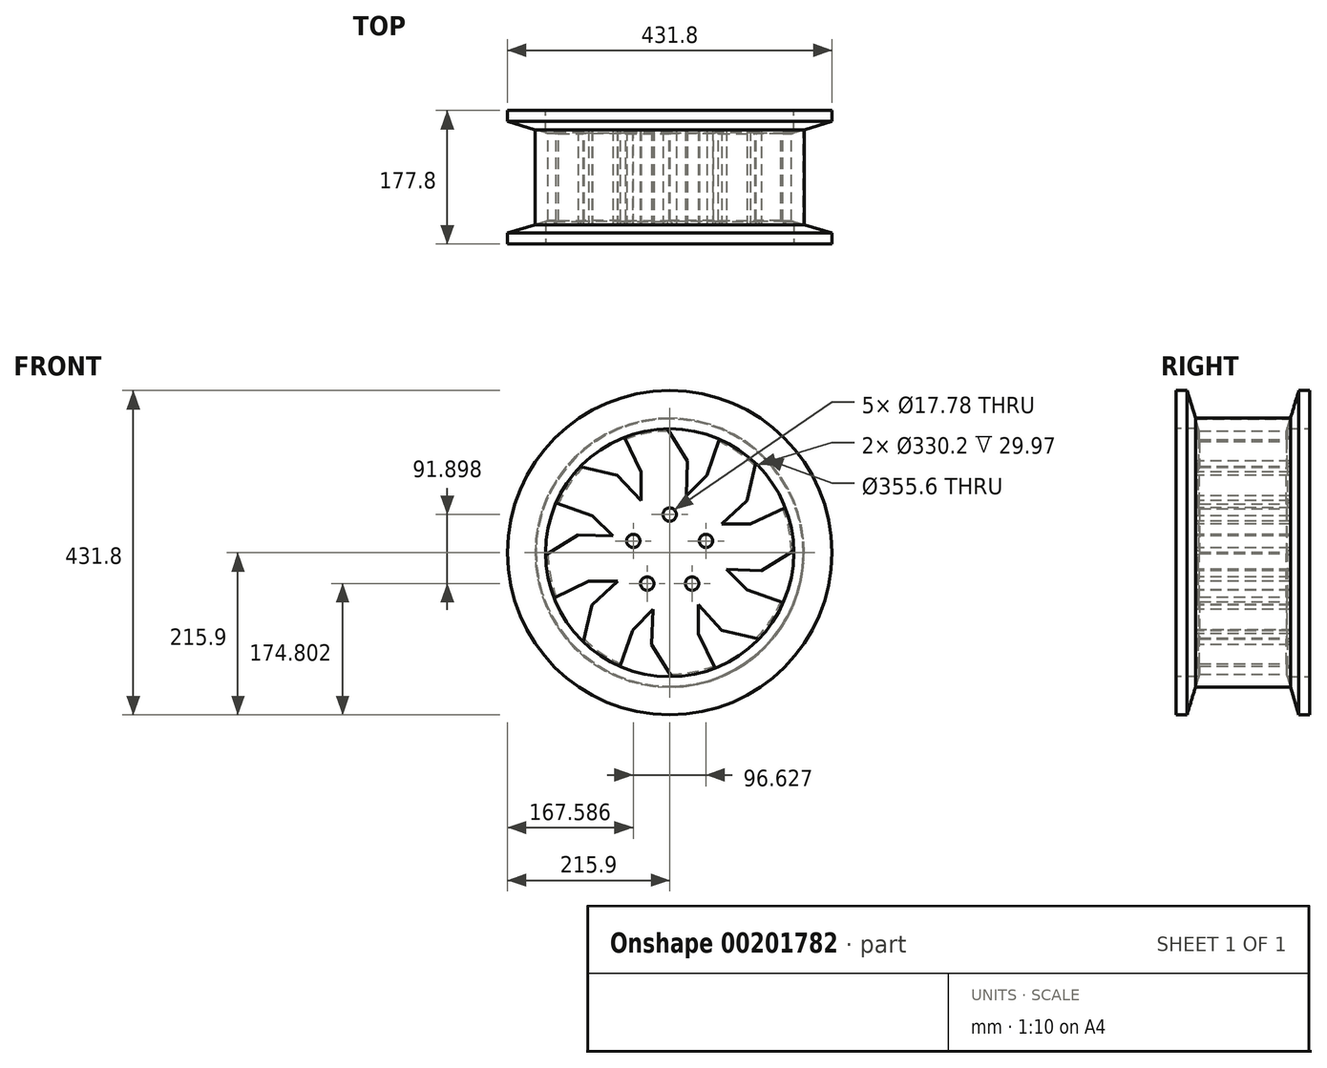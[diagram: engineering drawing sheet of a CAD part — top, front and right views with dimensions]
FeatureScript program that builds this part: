
annotation { "Feature Type Name" : "Feature", "Feature Type Description" : "" }
export const myFeature = defineFeature(function(context is Context, id is Id, definition is map)
    precondition{}
    {
        {
            var Q0;
            Q0=qCreatedBy(makeId("Front.planeOp"),FACE);
            var sketch = newSketch(context, id + "F0", { "sketchPlane" : qUnion([Q0])});
            skCircle(sketch, "E0", {"center": v(0, 0) * mm, "radius": 215.9 * mm});
            skSolve(sketch);
        }
        {
            var Q0;
            Q0 = qSketchRegion(id + "F0", true);
            extrude(context, id + "F1", {"entities" : qUnion([Q0]), "oppositeDirection" : true, "depth" : 177.8 * mm});
        }
        {
            var Q0;
            Q0=qCreatedBy(makeId("Right.planeOp"),FACE);
            var sketch = newSketch(context, id + "F2", { "sketchPlane" : qUnion([Q0])});
            skLineSegment(sketch, "E1", {"start": v(12.27, 222.89) * mm, "end": v(30.99, 161.77) * mm});
            skLineSegment(sketch, "E2", {"start": v(30.99, 161.77) * mm, "end": v(85.04, 161.77) * mm});
            skLineSegment(sketch, "E3", {"start": v(88.9, 247.97) * mm, "end": v(88.9, 109.84) * mm});
            skLineSegment(sketch, "E4", {"start": v(85.04, 161.77) * mm, "end": v(88.9, 161.77) * mm});
            skLineSegment(sketch, "E5", {"start": v(12.27, 222.89) * mm, "end": v(88.9, 222.89) * mm});
            skLineSegment(sketch, "E6.MirrorCS", {"start": v(165.53, 222.89) * mm, "end": v(88.9, 222.89) * mm});
            skLineSegment(sketch, "E7.MirrorCS", {"start": v(165.53, 222.89) * mm, "end": v(146.81, 161.77) * mm});
            skLineSegment(sketch, "E8.MirrorCS", {"start": v(146.81, 161.77) * mm, "end": v(92.76, 161.77) * mm});
            skLineSegment(sketch, "E9.MirrorCS", {"start": v(92.76, 161.77) * mm, "end": v(88.9, 161.77) * mm});
            skSolve(sketch);
        }
        {
            var Q0;
            Q0=qCreatedBy(makeId("Right.planeOp"),FACE);
            var sketch = newSketch(context, id + "F3", { "sketchPlane" : qUnion([Q0])});
            skLineSegment(sketch, "E10", {"start": v(0, 0) * mm, "end": v(269.37, 0) * mm});
            skSolve(sketch);
        }
        {
            var Q0;
            {var subQ0=sQuery(id+"F2.wireOp",EDGE,"E6.MirrorCS");Q0=makeQuery(id+"F2.imprint","IMPRINT",FACE,{"disambiguationData":[TD([[makeQuery(id+"F2.imprint","IMPRINT",EDGE,{"derivedFrom":subQ0}),1.0]])]});}
            var Q1;
            Q1=makeQuery(id+"F2.imprint","IMPRINT",FACE,{"disambiguationData":[TD([[makeQuery(id+"F2.imprint","IMPRINT",EDGE,{"derivedFrom":sQuery(id+"F2.wireOp",EDGE,"E1")}),1.0]])]});
            var Q2;
            Q2=sQuery(id+"F3.wireOp",EDGE,"E10");
            revolve(context, id + "F4", {"operationType" : NewBodyOperationType.REMOVE, "entities" : qUnion([Q0, Q1]), "axis" : qUnion([Q2]), "revolveType" : RevolveType.FULL, "oppositeDirection" : true});
        }
        {
            var Q0;
            Q0=makeQuery(id+"F1.opExtrude","CAP_FACE",FACE,{"disambiguationData":[OSD([sQuery(id+"F0.wireOp",EDGE,"E0")])],"isStart":true});
            var sketch = newSketch(context, id + "F5", { "sketchPlane" : qUnion([Q0])});
            skCircle(sketch, "E11", {"center": v(0, 0) * mm, "radius": 165.1 * mm});
            skSolve(sketch);
        }
        {
            var Q0;
            Q0 = qSketchRegion(id + "F5", true);
            extrude(context, id + "F6", {"entities" : qUnion([Q0]), "operationType" : NewBodyOperationType.REMOVE, "oppositeDirection" : true, "depth" : 25.4 * mm});
        }
        {
            var Q0;
            Q0=makeQuery(id+"F1.opExtrude","CAP_FACE",FACE,{"disambiguationData":[OSD([sQuery(id+"F0.wireOp",EDGE,"E0")])],"isStart":false});
            var sketch = newSketch(context, id + "F7", { "sketchPlane" : qUnion([Q0])});
            skCircle(sketch, "E12", {"center": v(0, 0) * mm, "radius": 165.1 * mm});
            skSolve(sketch);
        }
        {
            var Q0;
            Q0 = qSketchRegion(id + "F7", true);
            extrude(context, id + "F8", {"entities" : qUnion([Q0]), "operationType" : NewBodyOperationType.REMOVE, "oppositeDirection" : true, "depth" : 25.4 * mm});
        }
        {
            var Q0;
            Q0=makeQuery(id+"F6.boolean.opBoolean","COPY",FACE,{"derivedFrom":makeQuery(id+"F6.opExtrude","CAP_FACE",FACE,{"disambiguationData":[OSD([sQuery(id+"F5.wireOp",EDGE,"E11")])],"isStart":false})});
            var sketch = newSketch(context, id + "F9", { "sketchPlane" : qUnion([Q0])});
            skCircle(sketch, "E13", {"center": v(0, 50.8) * mm, "radius": 8.9 * mm});
            skCircle(sketch, "E14.1.0", {"center": v(-48.31, 15.7) * mm, "radius": 8.9 * mm});
            skCircle(sketch, "E14.2.0", {"center": v(-29.86, -41.1) * mm, "radius": 8.9 * mm});
            skCircle(sketch, "E14.3.0", {"center": v(29.86, -41.1) * mm, "radius": 8.9 * mm});
            skCircle(sketch, "E14.4.0", {"center": v(48.31, 15.7) * mm, "radius": 8.9 * mm});
            skPoint(sketch, "E14.center", {"position": v(0, 0) * mm});
            skSolve(sketch);
        }
        {
            var Q0;
            Q0 = qSketchRegion(id + "F9", true);
            extrude(context, id + "F10", {"entities" : qUnion([Q0]), "operationType" : NewBodyOperationType.REMOVE, "endBound" : BoundingType.THROUGH_ALL, "oppositeDirection" : true, "depth" : 25.4 * mm});
        }
        {
            var Q0;
            Q0=makeQuery(id+"F1.opExtrude","CAP_FACE",FACE,{"disambiguationData":[OSD([sQuery(id+"F0.wireOp",EDGE,"E0")])],"isStart":false});
            var sketch = newSketch(context, id + "F11", { "sketchPlane" : qUnion([Q0])});
            skCircle(sketch, "E15", {"center": v(0, 0) * mm, "radius": 177.8 * mm});
            skCircle(sketch, "E16", {"center": v(0, 0) * mm, "radius": 179.07 * mm});
            skSolve(sketch);
        }
        {
            var Q0;
            Q0 = qSketchRegion(id + "F11", true);
            extrude(context, id + "F12", {"entities" : qUnion([Q0]), "operationType" : NewBodyOperationType.ADD, "oppositeDirection" : true, "depth" : 158.75 * mm});
        }
        {
            var Q0;
            Q0=makeQuery(id+"F6.boolean.opBoolean","COPY",FACE,{"derivedFrom":makeQuery(id+"F6.opExtrude","CAP_FACE",FACE,{"disambiguationData":[OSD([sQuery(id+"F5.wireOp",EDGE,"E11")])],"isStart":false})});
            var sketch = newSketch(context, id + "F13", { "sketchPlane" : qUnion([Q0])});
            skLineSegment(sketch, "E17", {"start": v(-60.1, 153.77) * mm, "end": v(-37.94, 107.65) * mm});
            skLineSegment(sketch, "E18", {"start": v(-37.94, 69.14) * mm, "end": v(-69.59, 103.17) * mm});
            skLineSegment(sketch, "E19", {"start": v(-37.94, 107.65) * mm, "end": v(-37.94, 69.14) * mm});
            skLineSegment(sketch, "E20", {"start": v(-69.59, 103.17) * mm, "end": v(-118.77, 114.68) * mm});
            skArc(sketch, "E21", {"start": v(-118.77, 114.68) * mm, "mid": v(-91.55, 137.4) * mm, "end": v(-60.1, 153.77) * mm});
            skLineSegment(sketch, "E22.1.0", {"start": v(-122.16, 23.75) * mm, "end": v(-165.07, -2.9) * mm});
            skLineSegment(sketch, "E22.1.1", {"start": v(-102.95, 49.29) * mm, "end": v(-75.72, 22.06) * mm});
            skArc(sketch, "E22.1.2", {"start": v(-165.07, -2.9) * mm, "mid": v(-161.89, 32.42) * mm, "end": v(-151.23, 66.24) * mm});
            skLineSegment(sketch, "E22.1.3", {"start": v(-151.23, 66.24) * mm, "end": v(-102.95, 49.29) * mm});
            skLineSegment(sketch, "E22.1.4", {"start": v(-75.72, 22.06) * mm, "end": v(-122.16, 23.75) * mm});
            skLineSegment(sketch, "E22.2.0", {"start": v(-103.17, -69.59) * mm, "end": v(-114.68, -118.77) * mm});
            skLineSegment(sketch, "E22.2.1", {"start": v(-107.65, -37.94) * mm, "end": v(-69.14, -37.94) * mm});
            skArc(sketch, "E22.2.2", {"start": v(-114.68, -118.77) * mm, "mid": v(-137.4, -91.55) * mm, "end": v(-153.77, -60.1) * mm});
            skLineSegment(sketch, "E22.2.3", {"start": v(-153.77, -60.1) * mm, "end": v(-107.65, -37.94) * mm});
            skLineSegment(sketch, "E22.2.4", {"start": v(-69.14, -37.94) * mm, "end": v(-103.17, -69.59) * mm});
            skLineSegment(sketch, "E22.3.0", {"start": v(-23.75, -122.16) * mm, "end": v(2.9, -165.07) * mm});
            skLineSegment(sketch, "E22.3.1", {"start": v(-49.29, -102.95) * mm, "end": v(-22.06, -75.72) * mm});
            skArc(sketch, "E22.3.2", {"start": v(2.9, -165.07) * mm, "mid": v(-32.42, -161.89) * mm, "end": v(-66.24, -151.23) * mm});
            skLineSegment(sketch, "E22.3.3", {"start": v(-66.24, -151.23) * mm, "end": v(-49.29, -102.95) * mm});
            skLineSegment(sketch, "E22.3.4", {"start": v(-22.06, -75.72) * mm, "end": v(-23.75, -122.16) * mm});
            skLineSegment(sketch, "E22.4.0", {"start": v(69.59, -103.17) * mm, "end": v(118.77, -114.68) * mm});
            skLineSegment(sketch, "E22.4.1", {"start": v(37.94, -107.65) * mm, "end": v(37.94, -69.14) * mm});
            skArc(sketch, "E22.4.2", {"start": v(118.77, -114.68) * mm, "mid": v(91.55, -137.4) * mm, "end": v(60.1, -153.77) * mm});
            skLineSegment(sketch, "E22.4.3", {"start": v(60.1, -153.77) * mm, "end": v(37.94, -107.65) * mm});
            skLineSegment(sketch, "E22.4.4", {"start": v(37.94, -69.14) * mm, "end": v(69.59, -103.17) * mm});
            skLineSegment(sketch, "E22.5.0", {"start": v(122.16, -23.75) * mm, "end": v(165.07, 2.9) * mm});
            skLineSegment(sketch, "E22.5.1", {"start": v(102.95, -49.29) * mm, "end": v(75.72, -22.06) * mm});
            skArc(sketch, "E22.5.2", {"start": v(165.07, 2.9) * mm, "mid": v(161.89, -32.42) * mm, "end": v(151.23, -66.24) * mm});
            skLineSegment(sketch, "E22.5.3", {"start": v(151.23, -66.24) * mm, "end": v(102.95, -49.29) * mm});
            skLineSegment(sketch, "E22.5.4", {"start": v(75.72, -22.06) * mm, "end": v(122.16, -23.75) * mm});
            skLineSegment(sketch, "E22.6.0", {"start": v(103.17, 69.59) * mm, "end": v(114.68, 118.77) * mm});
            skLineSegment(sketch, "E22.6.1", {"start": v(107.65, 37.94) * mm, "end": v(69.14, 37.94) * mm});
            skArc(sketch, "E22.6.2", {"start": v(114.68, 118.77) * mm, "mid": v(137.4, 91.55) * mm, "end": v(153.77, 60.1) * mm});
            skLineSegment(sketch, "E22.6.3", {"start": v(153.77, 60.1) * mm, "end": v(107.65, 37.94) * mm});
            skLineSegment(sketch, "E22.6.4", {"start": v(69.14, 37.94) * mm, "end": v(103.17, 69.59) * mm});
            skLineSegment(sketch, "E22.7.0", {"start": v(23.75, 122.16) * mm, "end": v(-2.9, 165.07) * mm});
            skLineSegment(sketch, "E22.7.1", {"start": v(49.29, 102.95) * mm, "end": v(22.06, 75.72) * mm});
            skArc(sketch, "E22.7.2", {"start": v(-2.9, 165.07) * mm, "mid": v(32.42, 161.89) * mm, "end": v(66.24, 151.23) * mm});
            skLineSegment(sketch, "E22.7.3", {"start": v(66.24, 151.23) * mm, "end": v(49.29, 102.95) * mm});
            skLineSegment(sketch, "E22.7.4", {"start": v(22.06, 75.72) * mm, "end": v(23.75, 122.16) * mm});
            skSolve(sketch);
        }
        {
            var Q0;
            Q0 = qSketchRegion(id + "F13", true);
            extrude(context, id + "F14", {"entities" : qUnion([Q0]), "operationType" : NewBodyOperationType.REMOVE, "endBound" : BoundingType.THROUGH_ALL, "oppositeDirection" : true, "depth" : 25.4 * mm});
        }
        {
            var Q0;
            Q0=makeQuery(id+"F14.boolean.opBoolean","COPY",EDGE,{"derivedFrom":makeQuery(id+"F14.opExtrude","CAP_EDGE",EDGE,{"disambiguationData":[OSD([sQuery(id+"F13.wireOp",EDGE,"E20")])],"isStart":true})});
            var Q1;
            Q1=makeQuery(id+"F14.boolean.opBoolean","COPY",EDGE,{"derivedFrom":makeQuery(id+"F14.opExtrude","CAP_EDGE",EDGE,{"disambiguationData":[OSD([sQuery(id+"F13.wireOp",EDGE,"E18")])],"isStart":true})});
            var Q2;
            Q2=makeQuery(id+"F14.boolean.opBoolean","COPY",EDGE,{"derivedFrom":makeQuery(id+"F14.opExtrude","CAP_EDGE",EDGE,{"disambiguationData":[OSD([sQuery(id+"F13.wireOp",EDGE,"E19")])],"isStart":true})});
            var Q3;
            Q3=makeQuery(id+"F14.boolean.opBoolean","COPY",EDGE,{"derivedFrom":makeQuery(id+"F14.opExtrude","CAP_EDGE",EDGE,{"disambiguationData":[OSD([sQuery(id+"F13.wireOp",EDGE,"E17")])],"isStart":true})});
            var Q4;
            Q4=makeQuery(id+"F14.boolean.opBoolean","COPY",EDGE,{"derivedFrom":makeQuery(id+"F14.opExtrude","CAP_EDGE",EDGE,{"disambiguationData":[OSD([sQuery(id+"F13.wireOp",EDGE,"E22.7.0")])],"isStart":true})});
            var Q5;
            Q5=makeQuery(id+"F14.boolean.opBoolean","COPY",EDGE,{"derivedFrom":makeQuery(id+"F14.opExtrude","CAP_EDGE",EDGE,{"disambiguationData":[OSD([sQuery(id+"F13.wireOp",EDGE,"E22.7.4")])],"isStart":true})});
            var Q6;
            Q6=makeQuery(id+"F14.boolean.opBoolean","COPY",EDGE,{"derivedFrom":makeQuery(id+"F14.opExtrude","CAP_EDGE",EDGE,{"disambiguationData":[OSD([sQuery(id+"F13.wireOp",EDGE,"E22.7.1")])],"isStart":true})});
            var Q7;
            Q7=makeQuery(id+"F14.boolean.opBoolean","COPY",EDGE,{"derivedFrom":makeQuery(id+"F14.opExtrude","CAP_EDGE",EDGE,{"disambiguationData":[OSD([sQuery(id+"F13.wireOp",EDGE,"E22.7.3")])],"isStart":true})});
            var Q8;
            Q8=makeQuery(id+"F14.boolean.opBoolean","COPY",EDGE,{"derivedFrom":makeQuery(id+"F14.opExtrude","CAP_EDGE",EDGE,{"disambiguationData":[OSD([sQuery(id+"F13.wireOp",EDGE,"E22.6.4")])],"isStart":true})});
            var Q9;
            Q9=makeQuery(id+"F14.boolean.opBoolean","COPY",EDGE,{"derivedFrom":makeQuery(id+"F14.opExtrude","CAP_EDGE",EDGE,{"disambiguationData":[OSD([sQuery(id+"F13.wireOp",EDGE,"E22.6.1")])],"isStart":true})});
            var Q10;
            Q10=makeQuery(id+"F14.boolean.opBoolean","COPY",EDGE,{"derivedFrom":makeQuery(id+"F14.opExtrude","CAP_EDGE",EDGE,{"disambiguationData":[OSD([sQuery(id+"F13.wireOp",EDGE,"E22.6.3")])],"isStart":true})});
            var Q11;
            Q11=makeQuery(id+"F14.boolean.opBoolean","COPY",EDGE,{"derivedFrom":makeQuery(id+"F14.opExtrude","CAP_EDGE",EDGE,{"disambiguationData":[OSD([sQuery(id+"F13.wireOp",EDGE,"E22.6.0")])],"isStart":true})});
            var Q12;
            Q12=makeQuery(id+"F14.boolean.opBoolean","COPY",EDGE,{"derivedFrom":makeQuery(id+"F14.opExtrude","CAP_EDGE",EDGE,{"disambiguationData":[OSD([sQuery(id+"F13.wireOp",EDGE,"E22.5.0")])],"isStart":true})});
            var Q13;
            Q13=makeQuery(id+"F14.boolean.opBoolean","COPY",EDGE,{"derivedFrom":makeQuery(id+"F14.opExtrude","CAP_EDGE",EDGE,{"disambiguationData":[OSD([sQuery(id+"F13.wireOp",EDGE,"E22.5.4")])],"isStart":true})});
            var Q14;
            Q14=makeQuery(id+"F14.boolean.opBoolean","COPY",EDGE,{"derivedFrom":makeQuery(id+"F14.opExtrude","CAP_EDGE",EDGE,{"disambiguationData":[OSD([sQuery(id+"F13.wireOp",EDGE,"E22.5.1")])],"isStart":true})});
            var Q15;
            Q15=makeQuery(id+"F14.boolean.opBoolean","COPY",EDGE,{"derivedFrom":makeQuery(id+"F14.opExtrude","CAP_EDGE",EDGE,{"disambiguationData":[OSD([sQuery(id+"F13.wireOp",EDGE,"E22.5.3")])],"isStart":true})});
            var Q16;
            Q16=makeQuery(id+"F14.boolean.opBoolean","COPY",EDGE,{"derivedFrom":makeQuery(id+"F14.opExtrude","CAP_EDGE",EDGE,{"disambiguationData":[OSD([sQuery(id+"F13.wireOp",EDGE,"E22.4.0")])],"isStart":true})});
            var Q17;
            Q17=makeQuery(id+"F14.boolean.opBoolean","COPY",EDGE,{"derivedFrom":makeQuery(id+"F14.opExtrude","CAP_EDGE",EDGE,{"disambiguationData":[OSD([sQuery(id+"F13.wireOp",EDGE,"E22.4.4")])],"isStart":true})});
            var Q18;
            Q18=makeQuery(id+"F14.boolean.opBoolean","COPY",EDGE,{"derivedFrom":makeQuery(id+"F14.opExtrude","CAP_EDGE",EDGE,{"disambiguationData":[OSD([sQuery(id+"F13.wireOp",EDGE,"E22.4.1")])],"isStart":true})});
            var Q19;
            Q19=makeQuery(id+"F14.boolean.opBoolean","COPY",EDGE,{"derivedFrom":makeQuery(id+"F14.opExtrude","CAP_EDGE",EDGE,{"disambiguationData":[OSD([sQuery(id+"F13.wireOp",EDGE,"E22.4.3")])],"isStart":true})});
            var Q20;
            Q20=makeQuery(id+"F14.boolean.opBoolean","COPY",EDGE,{"derivedFrom":makeQuery(id+"F14.opExtrude","CAP_EDGE",EDGE,{"disambiguationData":[OSD([sQuery(id+"F13.wireOp",EDGE,"E22.3.0")])],"isStart":true})});
            var Q21;
            Q21=makeQuery(id+"F14.boolean.opBoolean","COPY",EDGE,{"derivedFrom":makeQuery(id+"F14.opExtrude","CAP_EDGE",EDGE,{"disambiguationData":[OSD([sQuery(id+"F13.wireOp",EDGE,"E22.3.4")])],"isStart":true})});
            var Q22;
            Q22=makeQuery(id+"F14.boolean.opBoolean","COPY",EDGE,{"derivedFrom":makeQuery(id+"F14.opExtrude","SWEPT_EDGE",EDGE,{"disambiguationData":[OSD([sQuery(id+"F13.wireOp",EDGE,"E22.3.1"),sQuery(id+"F13.wireOp",EDGE,"E22.3.3")])]})});
            var Q23;
            Q23=makeQuery(id+"F14.boolean.opBoolean","COPY",EDGE,{"derivedFrom":makeQuery(id+"F14.opExtrude","CAP_EDGE",EDGE,{"disambiguationData":[OSD([sQuery(id+"F13.wireOp",EDGE,"E22.3.3")])],"isStart":true})});
            var Q24;
            Q24=makeQuery(id+"F14.boolean.opBoolean","COPY",EDGE,{"derivedFrom":makeQuery(id+"F14.opExtrude","CAP_EDGE",EDGE,{"disambiguationData":[OSD([sQuery(id+"F13.wireOp",EDGE,"E22.2.0")])],"isStart":true})});
            var Q25;
            Q25=makeQuery(id+"F14.boolean.opBoolean","COPY",EDGE,{"derivedFrom":makeQuery(id+"F14.opExtrude","CAP_EDGE",EDGE,{"disambiguationData":[OSD([sQuery(id+"F13.wireOp",EDGE,"E22.2.4")])],"isStart":true})});
            var Q26;
            Q26=makeQuery(id+"F14.boolean.opBoolean","COPY",EDGE,{"derivedFrom":makeQuery(id+"F14.opExtrude","CAP_EDGE",EDGE,{"disambiguationData":[OSD([sQuery(id+"F13.wireOp",EDGE,"E22.2.1")])],"isStart":true})});
            var Q27;
            Q27=makeQuery(id+"F14.boolean.opBoolean","COPY",EDGE,{"derivedFrom":makeQuery(id+"F14.opExtrude","CAP_EDGE",EDGE,{"disambiguationData":[OSD([sQuery(id+"F13.wireOp",EDGE,"E22.2.3")])],"isStart":true})});
            var Q28;
            Q28=makeQuery(id+"F14.boolean.opBoolean","COPY",EDGE,{"derivedFrom":makeQuery(id+"F14.opExtrude","CAP_EDGE",EDGE,{"disambiguationData":[OSD([sQuery(id+"F13.wireOp",EDGE,"E22.1.0")])],"isStart":true})});
            var Q29;
            Q29=makeQuery(id+"F14.boolean.opBoolean","COPY",EDGE,{"derivedFrom":makeQuery(id+"F14.opExtrude","CAP_EDGE",EDGE,{"disambiguationData":[OSD([sQuery(id+"F13.wireOp",EDGE,"E22.1.4")])],"isStart":true})});
            var Q30;
            Q30=makeQuery(id+"F14.boolean.opBoolean","COPY",EDGE,{"derivedFrom":makeQuery(id+"F14.opExtrude","CAP_EDGE",EDGE,{"disambiguationData":[OSD([sQuery(id+"F13.wireOp",EDGE,"E22.1.1")])],"isStart":true})});
            var Q31;
            Q31=makeQuery(id+"F14.boolean.opBoolean","COPY",EDGE,{"derivedFrom":makeQuery(id+"F14.opExtrude","CAP_EDGE",EDGE,{"disambiguationData":[OSD([sQuery(id+"F13.wireOp",EDGE,"E22.1.3")])],"isStart":true})});
            chamfer(context, id + "F15", {"entities" : qUnion([Q0, Q1, Q2, Q3, Q4, Q5, Q6, Q7, Q8, Q9, Q10, Q11, Q12, Q13, Q14, Q15, Q16, Q17, Q18, Q19, Q20, Q21, Q22, Q23, Q24, Q25, Q26, Q27, Q28, Q29, Q30, Q31]), "width" : 5.08 * mm, "tangentPropagation" : true});
        }
    });
